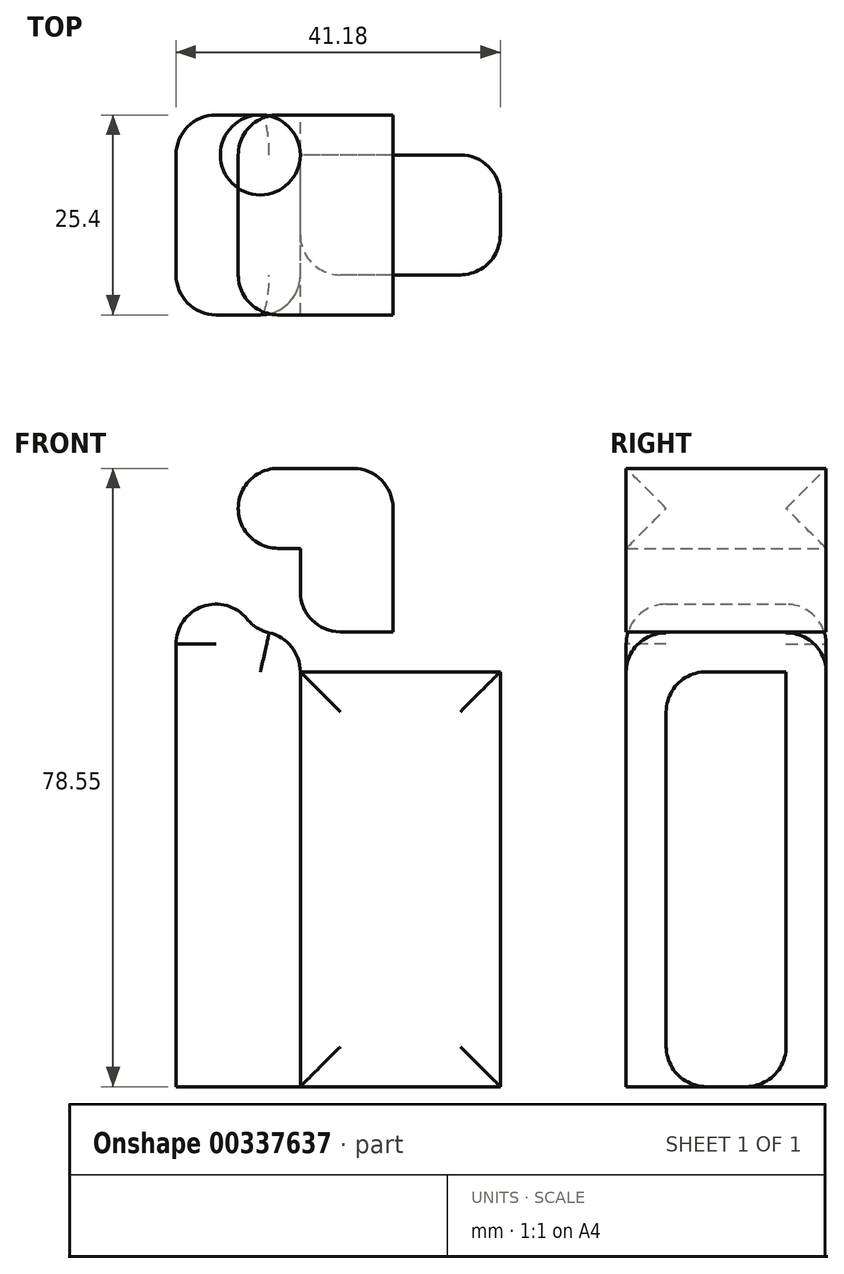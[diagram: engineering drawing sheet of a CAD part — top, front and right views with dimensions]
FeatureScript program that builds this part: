
annotation { "Feature Type Name" : "Feature", "Feature Type Description" : "" }
export const myFeature = defineFeature(function(context is Context, id is Id, definition is map)
    precondition{}
    {
        {
            var Q0;
            Q0=qCreatedBy(makeId("Front.planeOp"),FACE);
            var sketch = newSketch(context, id + "F0", { "sketchPlane" : qUnion([Q0])});
            skLineSegment(sketch, "E0.bottom", {"start": v(26.44, 35.28) * mm, "end": v(46.1, 35.28) * mm});
            skLineSegment(sketch, "E0.top", {"start": v(26.44, 56.05) * mm, "end": v(46.1, 56.05) * mm});
            skLineSegment(sketch, "E0.left", {"start": v(26.44, 35.28) * mm, "end": v(26.44, 56.05) * mm});
            skLineSegment(sketch, "E0.right", {"start": v(46.1, 35.28) * mm, "end": v(46.1, 56.05) * mm});
            skPoint(sketch, "E0.middle", {"position": v(36.27, 45.67) * mm});
            skLineSegment(sketch, "E1.bottom", {"start": v(34.33, 45.88) * mm, "end": v(18.55, 45.88) * mm});
            skLineSegment(sketch, "E1.top", {"start": v(34.33, -22.5) * mm, "end": v(18.55, -22.5) * mm});
            skLineSegment(sketch, "E1.left", {"start": v(34.33, 45.88) * mm, "end": v(34.33, -22.5) * mm});
            skLineSegment(sketch, "E1.right", {"start": v(18.55, 45.88) * mm, "end": v(18.55, -22.5) * mm});
            skPoint(sketch, "E1.middle", {"position": v(26.44, 11.7) * mm});
            skSolve(sketch);
        }
        {
            var Q0;
            {var subQ4=sQuery(id+"F0.wireOp",EDGE,"E1.top");Q0=makeQuery(id+"F0.imprint","IMPRINT",FACE,{"disambiguationData":[TD([[makeQuery(id+"F0.imprint","IMPRINT",EDGE,{"derivedFrom":subQ4}),-1.0]])]});}
            var Q1;
            {var subQ2=sQuery(id+"F0.wireOp",EDGE,"E0.top");Q1=makeQuery(id+"F0.imprint","IMPRINT",FACE,{"disambiguationData":[TD([[makeQuery(id+"F0.imprint","IMPRINT",EDGE,{"derivedFrom":subQ2}),-1.0]])]});}
            extrude(context, id + "F1", {"entities" : qUnion([Q0, Q1]), "depth" : 25.4 * mm});
        }
        {
            var Q0;
            {var subQ0=sQuery(id+"F0.wireOp",EDGE,"E1.left");Q0=makeQuery(id+"F1.opExtrude","CAP_EDGE",EDGE,{"disambiguationData":[OSD([subQ0]),TDD([makeQuery(id+"F0.imprint","IMPRINT",EDGE,{"disambiguationData":[TD([[makeQuery(id+"F0.imprint","INTERSECT",VERTEX,{"derivedFrom":[sQuery(id+"F0.wireOp",EDGE,"E1.top"),subQ0]}),1.0]])],"derivedFrom":subQ0})])],"isStart":false});}
            var Q1;
            Q1=makeQuery(id+"F1.opExtrude","CAP_EDGE",EDGE,{"disambiguationData":[OSD([sQuery(id+"F0.wireOp",EDGE,"E1.right")])],"isStart":true});
            var Q2;
            {var subQ0=sQuery(id+"F0.wireOp",EDGE,"E1.left");Q2=makeQuery(id+"F1.opExtrude","CAP_EDGE",EDGE,{"disambiguationData":[OSD([subQ0]),TDD([makeQuery(id+"F0.imprint","IMPRINT",EDGE,{"disambiguationData":[TD([[makeQuery(id+"F0.imprint","INTERSECT",VERTEX,{"derivedFrom":[sQuery(id+"F0.wireOp",EDGE,"E1.top"),subQ0]}),1.0]])],"derivedFrom":subQ0})])],"isStart":true});}
            var Q3;
            Q3=makeQuery(id+"F1.opExtrude","CAP_EDGE",EDGE,{"disambiguationData":[OSD([sQuery(id+"F0.wireOp",EDGE,"E1.right")])],"isStart":false});
            fillet(context, id + "F2", {"entities" : qUnion([Q0, Q1, Q2, Q3]), "radius" : 5.08 * mm, "tangentPropagation" : true, "allowEdgeOverflow" : false});
        }
        {
            var Q0;
            {var subQ0=sQuery(id+"F0.wireOp",EDGE,"E1.left");var subQ1=sQuery(id+"F0.wireOp",EDGE,"E0.bottom");Q0=makeQuery(id+"F1.opExtrude","SWEPT_EDGE",EDGE,{"disambiguationData":[OSD([subQ1,subQ0]),ownerDisambiguation([makeQuery(id+"F1.opExtrude","SWEPT_BODY",BODY,{"disambiguationData":[OSD([subQ1,sQuery(id+"F0.wireOp",EDGE,"E0.top"),sQuery(id+"F0.wireOp",EDGE,"E0.left"),sQuery(id+"F0.wireOp",EDGE,"E0.right"),sQuery(id+"F0.wireOp",EDGE,"E1.bottom"),subQ0])]})])]});}
            fillet(context, id + "F3", {"entities" : qUnion([Q0]), "radius" : 5.08 * mm, "tangentPropagation" : true, "allowEdgeOverflow" : false});
        }
        {
            var Q0;
            Q0=makeQuery(id+"F1.opExtrude","SWEPT_EDGE",EDGE,{"disambiguationData":[OSD([sQuery(id+"F0.wireOp",EDGE,"E0.top"),sQuery(id+"F0.wireOp",EDGE,"E0.left")])]});
            var Q1;
            {var subQ0=sQuery(id+"F0.wireOp",EDGE,"E1.bottom");var subQ1=sQuery(id+"F0.wireOp",EDGE,"E0.left");Q1=makeQuery(id+"F1.opExtrude","SWEPT_EDGE",EDGE,{"disambiguationData":[OSD([subQ1,subQ0]),ownerDisambiguation([makeQuery(id+"F1.opExtrude","SWEPT_BODY",BODY,{"disambiguationData":[OSD([sQuery(id+"F0.wireOp",EDGE,"E0.bottom"),subQ1,subQ0,sQuery(id+"F0.wireOp",EDGE,"E1.top"),sQuery(id+"F0.wireOp",EDGE,"E1.left"),sQuery(id+"F0.wireOp",EDGE,"E1.right")])]})])]});}
            var Q2;
            {var subQ0=sQuery(id+"F0.wireOp",EDGE,"E0.left");Q2=makeQuery(id+"F1.opExtrude","SWEPT_FACE",FACE,{"disambiguationData":[OSD([subQ0]),TDD([makeQuery(id+"F0.imprint","IMPRINT",EDGE,{"disambiguationData":[TD([[makeQuery(id+"F0.imprint","INTERSECT",VERTEX,{"derivedFrom":[sQuery(id+"F0.wireOp",EDGE,"E0.top"),subQ0]}),1.0]])],"derivedFrom":subQ0})])]});}
            fillet(context, id + "F4", {"entities" : qUnion([Q0, Q1, Q2]), "radius" : 5.08 * mm, "tangentPropagation" : true, "allowEdgeOverflow" : false});
        }
        {
            var Q0;
            Q0=makeQuery(id+"F1.opExtrude","SWEPT_EDGE",EDGE,{"disambiguationData":[OSD([sQuery(id+"F0.wireOp",EDGE,"E0.bottom"),sQuery(id+"F0.wireOp",EDGE,"E0.left")])]});
            fillet(context, id + "F5", {"entities" : qUnion([Q0]), "radius" : 5.08 * mm, "tangentPropagation" : true, "allowEdgeOverflow" : false});
        }
        {
            var Q0;
            Q0=makeQuery(id+"F1.opExtrude","SWEPT_EDGE",EDGE,{"disambiguationData":[OSD([sQuery(id+"F0.wireOp",EDGE,"E0.top"),sQuery(id+"F0.wireOp",EDGE,"E0.right")])]});
            fillet(context, id + "F6", {"entities" : qUnion([Q0]), "radius" : 5.08 * mm, "tangentPropagation" : true, "allowEdgeOverflow" : false});
        }
        {
            var Q0;
            {var subQ0=sQuery(id+"F0.wireOp",EDGE,"E1.left");Q0=makeQuery(id+"F1.opExtrude","SWEPT_FACE",FACE,{"disambiguationData":[OSD([subQ0]),TDD([makeQuery(id+"F0.imprint","IMPRINT",EDGE,{"disambiguationData":[TD([[makeQuery(id+"F0.imprint","INTERSECT",VERTEX,{"derivedFrom":[sQuery(id+"F0.wireOp",EDGE,"E1.top"),subQ0]}),1.0]])],"derivedFrom":subQ0})])]});}
            extrude(context, id + "F7", {"entities" : qUnion([Q0]), "depth" : 25.4 * mm});
        }
        {
            var Q0;
            {var subQ0=sQuery(id+"F0.wireOp",EDGE,"E1.left");var subQ1=makeQuery(id+"F0.imprint","IMPRINT",EDGE,{"disambiguationData":[TD([[makeQuery(id+"F0.imprint","INTERSECT",VERTEX,{"derivedFrom":[sQuery(id+"F0.wireOp",EDGE,"E1.top"),subQ0]}),1.0]])],"derivedFrom":subQ0});Q0=makeQuery(id+"F7.opExtrude","SWEPT_FACE",FACE,{"disambiguationData":[OSD([subQ0]),TDD([makeQuery(id+"F2.opFillet","BLEND_EDGE",EDGE,{"blendedFrom":[makeQuery(id+"F1.opExtrude","CAP_EDGE",EDGE,{"disambiguationData":[OSD([subQ0]),TDD([subQ1])],"isStart":false}),makeQuery(id+"F1.opExtrude","SWEPT_FACE",FACE,{"disambiguationData":[OSD([subQ0]),TDD([subQ1])]})],"blendedInto":[makeQuery(id+"F1.opExtrude","SWEPT_FACE",FACE,{"disambiguationData":[OSD([subQ0]),TDD([subQ1])]})]})])]});}
            var Q1;
            {var subQ0=sQuery(id+"F0.wireOp",EDGE,"E1.left");var subQ1=makeQuery(id+"F0.imprint","IMPRINT",EDGE,{"disambiguationData":[TD([[makeQuery(id+"F0.imprint","INTERSECT",VERTEX,{"derivedFrom":[sQuery(id+"F0.wireOp",EDGE,"E1.top"),subQ0]}),1.0]])],"derivedFrom":subQ0});Q1=makeQuery(id+"F2.opFillet","BLEND_EDGE",EDGE,{"blendedFrom":[makeQuery(id+"F1.opExtrude","CAP_EDGE",EDGE,{"disambiguationData":[OSD([subQ0]),TDD([subQ1])],"isStart":false}),makeQuery(id+"F1.opExtrude","SWEPT_FACE",FACE,{"disambiguationData":[OSD([subQ0]),TDD([subQ1])]})],"blendedInto":[makeQuery(id+"F1.opExtrude","SWEPT_FACE",FACE,{"disambiguationData":[OSD([subQ0]),TDD([subQ1])]})]});}
            fillet(context, id + "F8", {"entities" : qUnion([Q0, Q1]), "radius" : 5.08 * mm, "tangentPropagation" : true, "allowEdgeOverflow" : false});
        }
        {
            var Q0;
            {var subQ0=sQuery(id+"F0.wireOp",EDGE,"E1.left");var subQ1=makeQuery(id+"F0.imprint","IMPRINT",EDGE,{"disambiguationData":[TD([[makeQuery(id+"F0.imprint","INTERSECT",VERTEX,{"derivedFrom":[sQuery(id+"F0.wireOp",EDGE,"E1.top"),subQ0]}),1.0]])],"derivedFrom":subQ0});Q0=makeQuery(id+"F2.opFillet","BLEND_EDGE",EDGE,{"blendedFrom":[makeQuery(id+"F1.opExtrude","CAP_EDGE",EDGE,{"disambiguationData":[OSD([subQ0]),TDD([subQ1])],"isStart":true}),makeQuery(id+"F1.opExtrude","SWEPT_FACE",FACE,{"disambiguationData":[OSD([subQ0]),TDD([subQ1])]})],"blendedInto":[makeQuery(id+"F1.opExtrude","SWEPT_FACE",FACE,{"disambiguationData":[OSD([subQ0]),TDD([subQ1])]})]});}
            var Q1;
            {var subQ0=sQuery(id+"F0.wireOp",EDGE,"E1.left");var subQ1=makeQuery(id+"F0.imprint","IMPRINT",EDGE,{"disambiguationData":[TD([[makeQuery(id+"F0.imprint","INTERSECT",VERTEX,{"derivedFrom":[sQuery(id+"F0.wireOp",EDGE,"E1.top"),subQ0]}),1.0]])],"derivedFrom":subQ0});Q1=makeQuery(id+"F7.opExtrude","CAP_EDGE",EDGE,{"disambiguationData":[OSD([subQ0]),TDD([makeQuery(id+"F2.opFillet","BLEND_EDGE",EDGE,{"blendedFrom":[makeQuery(id+"F1.opExtrude","CAP_EDGE",EDGE,{"disambiguationData":[OSD([subQ0]),TDD([subQ1])],"isStart":true}),makeQuery(id+"F1.opExtrude","SWEPT_FACE",FACE,{"disambiguationData":[OSD([subQ0]),TDD([subQ1])]})],"blendedInto":[makeQuery(id+"F1.opExtrude","SWEPT_FACE",FACE,{"disambiguationData":[OSD([subQ0]),TDD([subQ1])]})]})])],"isStart":false});}
            var Q2;
            {var subQ0=sQuery(id+"F0.wireOp",EDGE,"E1.left");var subQ1=sQuery(id+"F0.wireOp",EDGE,"E0.bottom");var subQ3=makeQuery(id+"F0.imprint","IMPRINT",EDGE,{"disambiguationData":[TD([[makeQuery(id+"F0.imprint","INTERSECT",VERTEX,{"derivedFrom":[sQuery(id+"F0.wireOp",EDGE,"E1.top"),subQ0]}),1.0]])],"derivedFrom":subQ0});Q2=makeQuery(id+"F7.opExtrude","SWEPT_EDGE",EDGE,{"disambiguationData":[OSD([subQ1,subQ0]),TDD([makeQuery(id+"F2.opFillet","BLEND_VERTEX",VERTEX,{"blendedFrom":[makeQuery(id+"F1.opExtrude","CAP_EDGE",EDGE,{"disambiguationData":[OSD([subQ0]),TDD([subQ3])],"isStart":true}),makeQuery(id+"F1.opExtrude","SWEPT_FACE",FACE,{"disambiguationData":[OSD([subQ1]),TDD([makeQuery(id+"F0.imprint","IMPRINT",EDGE,{"disambiguationData":[TD([[makeQuery(id+"F0.imprint","INTERSECT",VERTEX,{"derivedFrom":[subQ1,sQuery(id+"F0.wireOp",EDGE,"E0.left")]}),-1.0]])],"derivedFrom":subQ1})])]}),makeQuery(id+"F1.opExtrude","SWEPT_FACE",FACE,{"disambiguationData":[OSD([subQ0]),TDD([subQ3])]})],"blendedInto":[makeQuery(id+"F1.opExtrude","SWEPT_FACE",FACE,{"disambiguationData":[OSD([subQ1]),TDD([makeQuery(id+"F0.imprint","IMPRINT",EDGE,{"disambiguationData":[TD([[makeQuery(id+"F0.imprint","INTERSECT",VERTEX,{"derivedFrom":[subQ1,sQuery(id+"F0.wireOp",EDGE,"E0.left")]}),-1.0]])],"derivedFrom":subQ1})])]}),makeQuery(id+"F1.opExtrude","SWEPT_FACE",FACE,{"disambiguationData":[OSD([subQ0]),TDD([subQ3])]})]})])]});}
            var Q3;
            {var subQ0=sQuery(id+"F0.wireOp",EDGE,"E1.left");var subQ1=sQuery(id+"F0.wireOp",EDGE,"E1.top");var subQ2=makeQuery(id+"F0.imprint","IMPRINT",EDGE,{"disambiguationData":[TD([[makeQuery(id+"F0.imprint","INTERSECT",VERTEX,{"derivedFrom":[subQ1,subQ0]}),1.0]])],"derivedFrom":subQ0});Q3=makeQuery(id+"F7.opExtrude","SWEPT_EDGE",EDGE,{"disambiguationData":[OSD([subQ1,subQ0]),TDD([makeQuery(id+"F2.opFillet","BLEND_VERTEX",VERTEX,{"blendedFrom":[makeQuery(id+"F1.opExtrude","CAP_EDGE",EDGE,{"disambiguationData":[OSD([subQ0]),TDD([subQ2])],"isStart":true}),makeQuery(id+"F1.opExtrude","SWEPT_FACE",FACE,{"disambiguationData":[OSD([subQ1])]}),makeQuery(id+"F1.opExtrude","SWEPT_FACE",FACE,{"disambiguationData":[OSD([subQ0]),TDD([subQ2])]})],"blendedInto":[makeQuery(id+"F1.opExtrude","SWEPT_FACE",FACE,{"disambiguationData":[OSD([subQ1])]}),makeQuery(id+"F1.opExtrude","SWEPT_FACE",FACE,{"disambiguationData":[OSD([subQ0]),TDD([subQ2])]})]})])]});}
            fillet(context, id + "F9", {"entities" : qUnion([Q0, Q1, Q2, Q3]), "radius" : 5.08 * mm, "tangentPropagation" : true, "allowEdgeOverflow" : false});
        }
        {
            var Q0;
            {var subQ0=sQuery(id+"F0.wireOp",EDGE,"E1.right");var subQ1=sQuery(id+"F0.wireOp",EDGE,"E1.bottom");var subQ2=sQuery(id+"F0.wireOp",EDGE,"E0.left");Q0=makeQuery(id+"F4.opFillet","BLEND_EDGE",EDGE,{"blendedFrom":[makeQuery(id+"F1.opExtrude","SWEPT_EDGE",EDGE,{"disambiguationData":[OSD([subQ2,subQ1]),ownerDisambiguation([makeQuery(id+"F1.opExtrude","SWEPT_BODY",BODY,{"disambiguationData":[OSD([sQuery(id+"F0.wireOp",EDGE,"E0.bottom"),subQ2,subQ1,sQuery(id+"F0.wireOp",EDGE,"E1.top"),sQuery(id+"F0.wireOp",EDGE,"E1.left"),subQ0])]})])]}),makeQuery(id+"F1.opExtrude","SWEPT_FACE",FACE,{"disambiguationData":[OSD([subQ1]),TDD([makeQuery(id+"F0.imprint","IMPRINT",EDGE,{"disambiguationData":[TD([[makeQuery(id+"F0.imprint","INTERSECT",VERTEX,{"derivedFrom":[subQ1,subQ0]}),1.0]])],"derivedFrom":subQ1})])]})],"blendedInto":[makeQuery(id+"F1.opExtrude","SWEPT_FACE",FACE,{"disambiguationData":[OSD([subQ1]),TDD([makeQuery(id+"F0.imprint","IMPRINT",EDGE,{"disambiguationData":[TD([[makeQuery(id+"F0.imprint","INTERSECT",VERTEX,{"derivedFrom":[subQ1,subQ0]}),1.0]])],"derivedFrom":subQ1})])]})]});}
            var Q1;
            Q1=makeQuery(id+"F1.opExtrude","SWEPT_EDGE",EDGE,{"disambiguationData":[OSD([sQuery(id+"F0.wireOp",EDGE,"E1.bottom"),sQuery(id+"F0.wireOp",EDGE,"E1.right")])]});
            var Q2;
            {var subQ0=sQuery(id+"F0.wireOp",EDGE,"E0.left");var subQ1=sQuery(id+"F0.wireOp",EDGE,"E0.top");Q2=makeQuery(id+"F4.opFillet","BLEND_EDGE",EDGE,{"blendedFrom":[makeQuery(id+"F1.opExtrude","SWEPT_EDGE",EDGE,{"disambiguationData":[OSD([subQ1,subQ0])]}),makeQuery(id+"F1.opExtrude","SWEPT_FACE",FACE,{"disambiguationData":[OSD([subQ0]),TDD([makeQuery(id+"F0.imprint","IMPRINT",EDGE,{"disambiguationData":[TD([[makeQuery(id+"F0.imprint","INTERSECT",VERTEX,{"derivedFrom":[subQ1,subQ0]}),1.0]])],"derivedFrom":subQ0})])]})],"blendedInto":[makeQuery(id+"F1.opExtrude","SWEPT_FACE",FACE,{"disambiguationData":[OSD([subQ0]),TDD([makeQuery(id+"F0.imprint","IMPRINT",EDGE,{"disambiguationData":[TD([[makeQuery(id+"F0.imprint","INTERSECT",VERTEX,{"derivedFrom":[subQ1,subQ0]}),1.0]])],"derivedFrom":subQ0})])]})]});}
            var Q3;
            {var subQ0=sQuery(id+"F0.wireOp",EDGE,"E0.left");var subQ1=sQuery(id+"F0.wireOp",EDGE,"E0.bottom");var subQ2=sQuery(id+"F0.wireOp",EDGE,"E1.bottom");Q3=makeQuery(id+"F4.opFillet","BLEND_EDGE",EDGE,{"blendedFrom":[makeQuery(id+"F1.opExtrude","SWEPT_EDGE",EDGE,{"disambiguationData":[OSD([subQ0,subQ2]),ownerDisambiguation([makeQuery(id+"F1.opExtrude","SWEPT_BODY",BODY,{"disambiguationData":[OSD([subQ1,subQ0,subQ2,sQuery(id+"F0.wireOp",EDGE,"E1.top"),sQuery(id+"F0.wireOp",EDGE,"E1.left"),sQuery(id+"F0.wireOp",EDGE,"E1.right")])]})])]}),makeQuery(id+"F1.opExtrude","SWEPT_FACE",FACE,{"disambiguationData":[OSD([subQ0]),TDD([makeQuery(id+"F0.imprint","IMPRINT",EDGE,{"disambiguationData":[TD([[makeQuery(id+"F0.imprint","INTERSECT",VERTEX,{"derivedFrom":[subQ1,subQ0]}),-1.0]])],"derivedFrom":subQ0})])]})],"blendedInto":[makeQuery(id+"F1.opExtrude","SWEPT_FACE",FACE,{"disambiguationData":[OSD([subQ0]),TDD([makeQuery(id+"F0.imprint","IMPRINT",EDGE,{"disambiguationData":[TD([[makeQuery(id+"F0.imprint","INTERSECT",VERTEX,{"derivedFrom":[subQ1,subQ0]}),-1.0]])],"derivedFrom":subQ0})])]})]});}
            fillet(context, id + "F10", {"entities" : qUnion([Q0, Q1, Q2, Q3]), "radius" : 5.08 * mm, "tangentPropagation" : true, "allowEdgeOverflow" : false});
        }
    });
